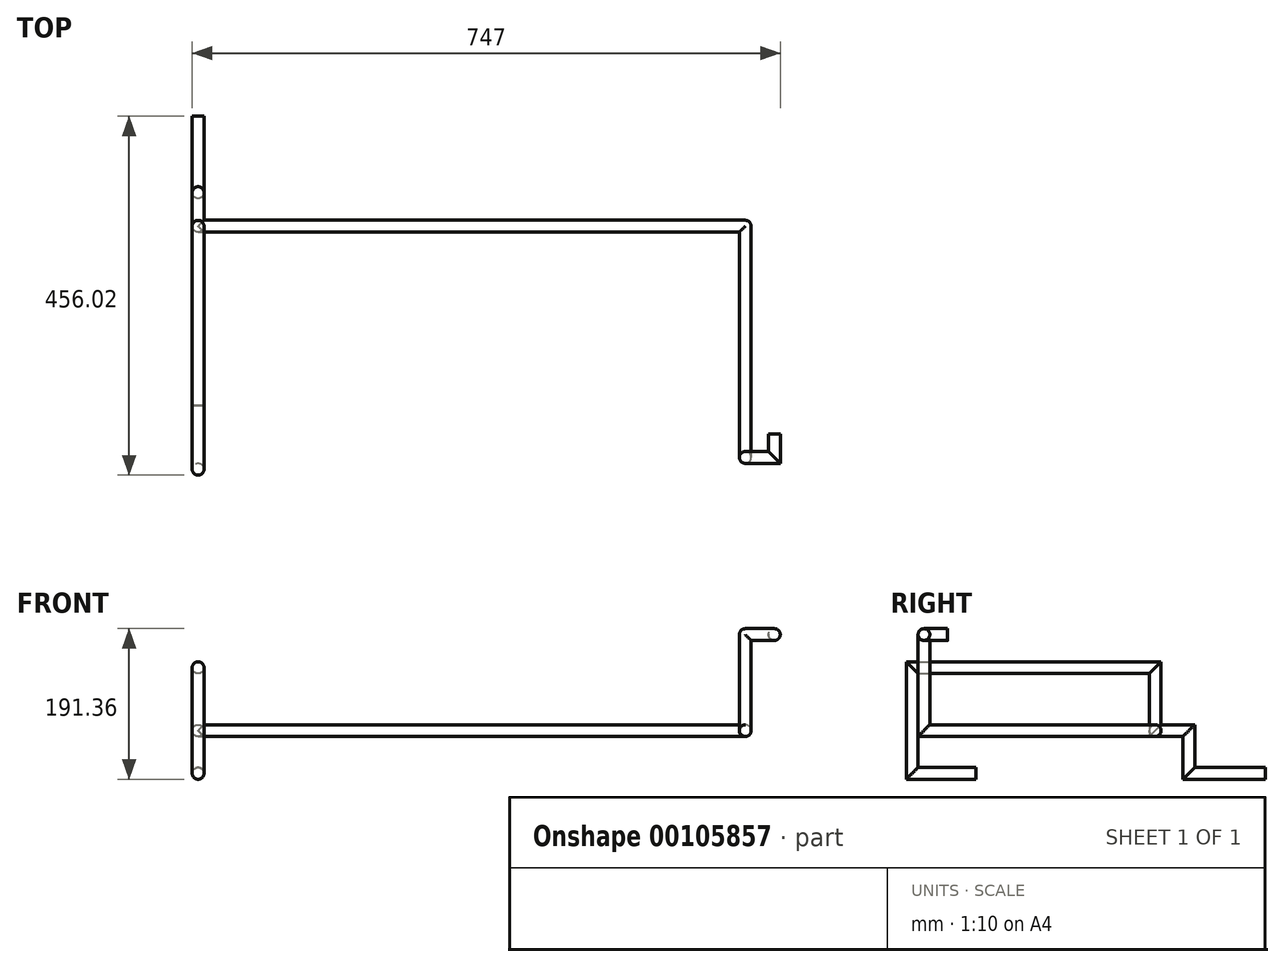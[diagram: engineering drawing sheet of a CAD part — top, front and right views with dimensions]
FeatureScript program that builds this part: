
annotation { "Feature Type Name" : "Feature", "Feature Type Description" : "" }
export const myFeature = defineFeature(function(context is Context, id is Id, definition is map)
    precondition{}
    {
        {
            var Q0;
            Q0=qCreatedBy(makeId("Front.planeOp"),FACE);
            var sketch = newSketch(context, id + "F0", { "sketchPlane" : qUnion([Q0])});
            skCircle(sketch, "E0", {"center": v(0, 0) * mm, "radius": 7.5 * mm});
            skSolve(sketch);
        }
        {
            var Q0;
            Q0=qCreatedBy(makeId("Right.planeOp"),FACE);
            var sketch = newSketch(context, id + "F1", { "sketchPlane" : qUnion([Q0])});
            skLineSegment(sketch, "E1", {"start": v(-80.78, 0) * mm, "end": v(0, 0) * mm});
            skLineSegment(sketch, "E2", {"start": v(-80.78, 0) * mm, "end": v(-80.78, 134.38) * mm});
            skLineSegment(sketch, "E3", {"start": v(-80.78, 134.38) * mm, "end": v(228, 134.38) * mm});
            skLineSegment(sketch, "E4", {"start": v(228, 134.38) * mm, "end": v(228, 54.38) * mm});
            skLineSegment(sketch, "E5", {"start": v(228, 54.38) * mm, "end": v(270.74, 54.38) * mm});
            skLineSegment(sketch, "E6", {"start": v(270.74, 54.38) * mm, "end": v(270.74, 0) * mm});
            skLineSegment(sketch, "E7", {"start": v(270.74, 0) * mm, "end": v(367.74, 0) * mm});
            skSolve(sketch);
        }
        {
            var Q0;
            Q0=makeQuery(id+"F0.imprint","IMPRINT",FACE,{"disambiguationData":[TD([[makeQuery(id+"F0.imprint","IMPRINT",EDGE,{"derivedFrom":sQuery(id+"F0.wireOp",EDGE,"E0")}),1.0]])]});
            var Q1;
            Q1=sQuery(id+"F1.wireOp",EDGE,"E1");
            var Q2;
            Q2=sQuery(id+"F1.wireOp",EDGE,"E2");
            var Q3;
            Q3=sQuery(id+"F1.wireOp",EDGE,"E3");
            var Q4;
            Q4=sQuery(id+"F1.wireOp",EDGE,"E4");
            var Q5;
            Q5=sQuery(id+"F1.wireOp",EDGE,"E5");
            var Q6;
            Q6=sQuery(id+"F1.wireOp",EDGE,"E6");
            var Q7;
            Q7=sQuery(id+"F1.wireOp",EDGE,"E7");
            sweep(context, id + "F2", {"profiles" : qUnion([Q0]), "path" : qUnion([Q1, Q2, Q3, Q4, Q5, Q6, Q7])});
        }
        {
            var Q0;
            Q0=qCreatedBy(makeId("Right.planeOp"),FACE);
            var sketch = newSketch(context, id + "F3", { "sketchPlane" : qUnion([Q0])});
            skCircle(sketch, "E8", {"center": v(228, 54.38) * mm, "radius": 7.5 * mm});
            skSolve(sketch);
        }
        {
            var Q0;
            Q0=qCreatedBy(makeId("Front.planeOp"),FACE);
            var sketch = newSketch(context, id + "F4", { "sketchPlane" : qUnion([Q0])});
            skLineSegment(sketch, "E9", {"start": v(0, 0) * mm, "end": v(695, 0) * mm});
            skSolve(sketch);
        }
        {
            var Q0;
            Q0 = qSketchRegion(id + "F3", true);
            var Q1;
            Q1=sQuery(id+"F4.wireOp",EDGE,"E9");
            sweep(context, id + "F5", {"operationType" : NewBodyOperationType.ADD, "profiles" : qUnion([Q0]), "path" : qUnion([Q1])});
        }
        {
            var Q0;
            Q0=qCreatedBy(makeId("Front.planeOp"),FACE);
            cPlane(context, id + "F6", {"entities" : qUnion([Q0]), "cplaneType" : CPlaneType.OFFSET, "offset" : 228 * mm, "oppositeDirection" : true, "width" : 150 * mm, "height" : 150 * mm});
        }
        {
            var Q0;
            Q0=qCreatedBy(id+"F6.planeOp",FACE);
            var sketch = newSketch(context, id + "F7", { "sketchPlane" : qUnion([Q0])});
            skCircle(sketch, "E10", {"center": v(695, 54.38) * mm, "radius": 7.5 * mm});
            skSolve(sketch);
        }
        {
            var Q0;
            Q0=qCreatedBy(makeId("Right.planeOp"),FACE);
            var sketch = newSketch(context, id + "F8", { "sketchPlane" : qUnion([Q0])});
            skLineSegment(sketch, "E11", {"start": v(228, 54.38) * mm, "end": v(-65.73, 54.38) * mm});
            skLineSegment(sketch, "E12", {"start": v(-65.73, 54.38) * mm, "end": v(-65.73, 176.36) * mm});
            skSolve(sketch);
        }
        {
            var Q0;
            Q0=makeQuery(id+"F7.imprint","IMPRINT",FACE,{"disambiguationData":[TD([[makeQuery(id+"F7.imprint","IMPRINT",EDGE,{"derivedFrom":sQuery(id+"F7.wireOp",EDGE,"E10")}),1.0]])]});
            var Q1;
            Q1=sQuery(id+"F8.wireOp",EDGE,"E11");
            var Q2;
            Q2=sQuery(id+"F8.wireOp",EDGE,"E12");
            sweep(context, id + "F9", {"operationType" : NewBodyOperationType.ADD, "profiles" : qUnion([Q0]), "path" : qUnion([Q1, Q2])});
        }
        {
            var Q0;
            Q0=qCreatedBy(makeId("Right.planeOp"),FACE);
            cPlane(context, id + "F10", {"entities" : qUnion([Q0]), "cplaneType" : CPlaneType.OFFSET, "offset" : 695 * mm, "width" : 150 * mm, "height" : 150 * mm});
        }
        {
            var Q0;
            Q0=qCreatedBy(id+"F10.planeOp",FACE);
            var sketch = newSketch(context, id + "F11", { "sketchPlane" : qUnion([Q0])});
            skCircle(sketch, "E13", {"center": v(-65.73, 176.36) * mm, "radius": 7.5 * mm});
            skSolve(sketch);
        }
        {
            var Q0;
            Q0=qCreatedBy(makeId("Top.planeOp"),FACE);
            var sketch = newSketch(context, id + "F12", { "sketchPlane" : qUnion([Q0])});
            skLineSegment(sketch, "E14", {"start": v(695, -65.73) * mm, "end": v(732, -65.73) * mm});
            skLineSegment(sketch, "E15", {"start": v(732, -65.73) * mm, "end": v(732, -35.73) * mm});
            skSolve(sketch);
        }
        {
            var Q0;
            Q0=makeQuery(id+"F11.imprint","IMPRINT",FACE,{"disambiguationData":[TD([[makeQuery(id+"F11.imprint","IMPRINT",EDGE,{"derivedFrom":sQuery(id+"F11.wireOp",EDGE,"E13")}),1.0]])]});
            var Q1;
            Q1=sQuery(id+"F12.wireOp",EDGE,"E14");
            var Q2;
            Q2=sQuery(id+"F12.wireOp",EDGE,"E15");
            sweep(context, id + "F13", {"operationType" : NewBodyOperationType.ADD, "profiles" : qUnion([Q0]), "path" : qUnion([Q1, Q2])});
        }
        {
            var Q0;
            Q0=makeQuery(id+"F9.opSweep","CAP_FACE",FACE,{"disambiguationData":[OSD([sQuery(id+"F7.wireOp",EDGE,"E10"),sQuery(id+"F8.wireOp",VERTEX,"E12.end")])],"isStart":false});
            var Q1;
            Q1=makeQuery(id+"F13.boolean.opBoolean","INTERSECT",EDGE,{"derivedFrom":[makeQuery(id+"F9.opSweep","CAP_FACE",FACE,{"disambiguationData":[OSD([sQuery(id+"F7.wireOp",EDGE,"E10"),sQuery(id+"F8.wireOp",VERTEX,"E12.end")])],"isStart":false}),makeQuery(id+"F13.opSweep","CAP_FACE",FACE,{"disambiguationData":[OSD([sQuery(id+"F11.wireOp",EDGE,"E13"),sQuery(id+"F12.wireOp",VERTEX,"E14.start")])],"isStart":true})]});
            revolve(context, id + "F14", {"operationType" : NewBodyOperationType.ADD, "entities" : qUnion([Q0]), "axis" : qUnion([Q1]), "revolveType" : RevolveType.FULL});
        }
        {
            var Q0;
            Q0=makeQuery(id+"F9.opSweep","CAP_FACE",FACE,{"disambiguationData":[OSD([sQuery(id+"F7.wireOp",EDGE,"E10"),sQuery(id+"F8.wireOp",VERTEX,"E11.start")])],"isStart":true});
            var Q1;
            Q1=makeQuery(id+"F9.boolean.opBoolean","INTERSECT",EDGE,{"derivedFrom":[makeQuery(id+"F5.opSweep","CAP_FACE",FACE,{"disambiguationData":[OSD([sQuery(id+"F3.wireOp",EDGE,"E8"),sQuery(id+"F4.wireOp",VERTEX,"E9.end")])],"isStart":false}),makeQuery(id+"F9.opSweep","CAP_FACE",FACE,{"disambiguationData":[OSD([sQuery(id+"F7.wireOp",EDGE,"E10"),sQuery(id+"F8.wireOp",VERTEX,"E11.start")])],"isStart":true})]});
            revolve(context, id + "F15", {"operationType" : NewBodyOperationType.ADD, "entities" : qUnion([Q0]), "axis" : qUnion([Q1]), "revolveType" : RevolveType.FULL});
        }
    });
